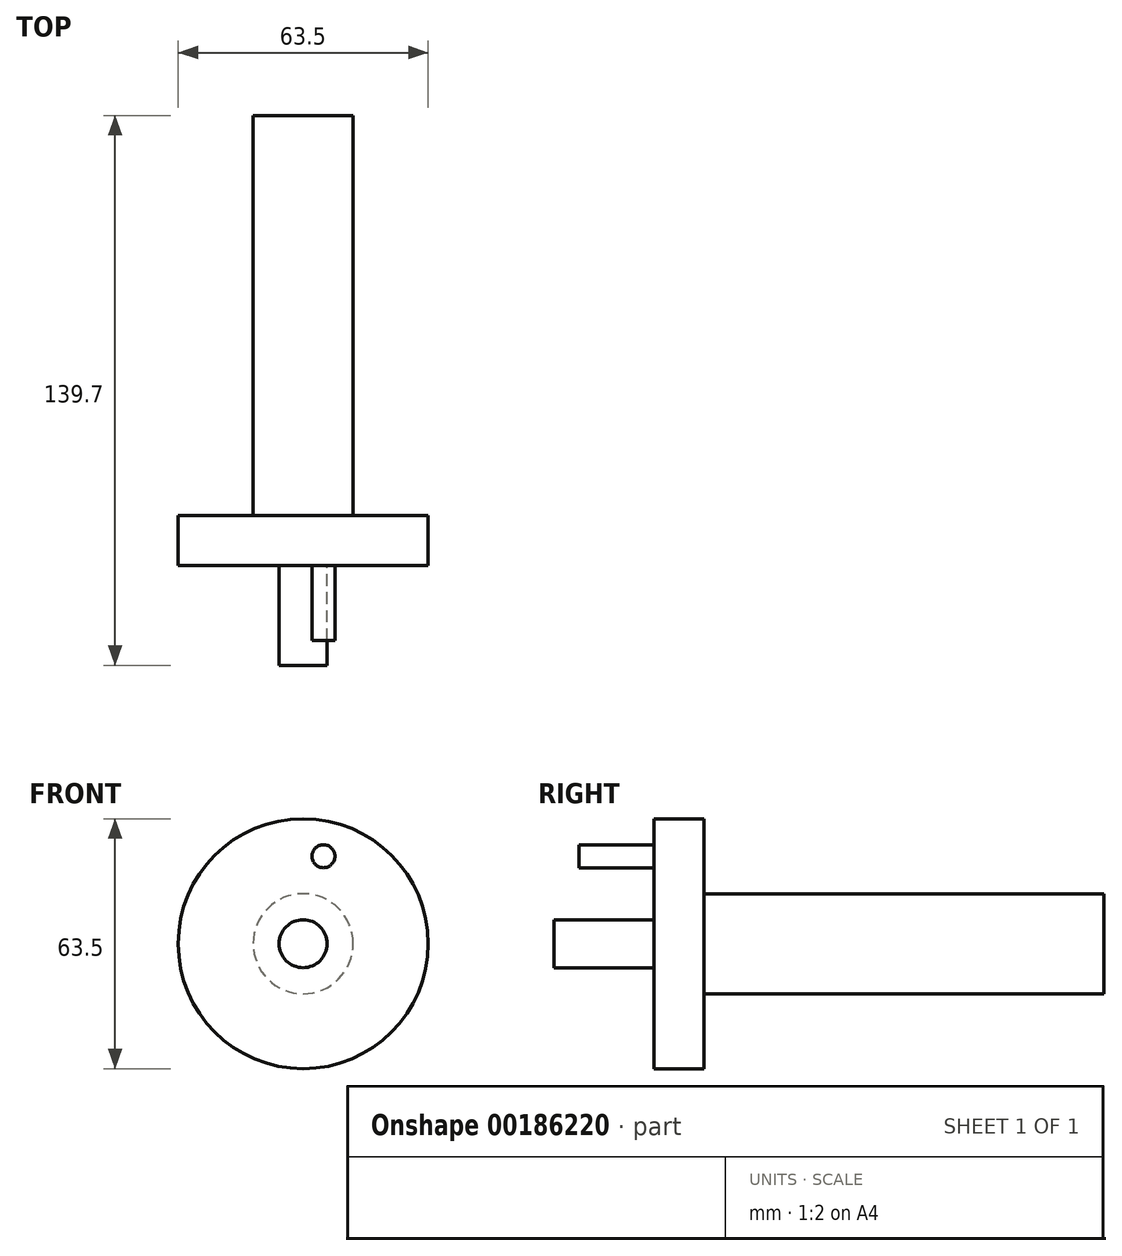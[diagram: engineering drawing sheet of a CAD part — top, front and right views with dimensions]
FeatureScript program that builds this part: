
annotation { "Feature Type Name" : "Feature", "Feature Type Description" : "" }
export const myFeature = defineFeature(function(context is Context, id is Id, definition is map)
    precondition{}
    {
        {
            var Q0;
            Q0=qCreatedBy(makeId("Front.planeOp"),FACE);
            var sketch = newSketch(context, id + "F0", { "sketchPlane" : qUnion([Q0])});
            skCircle(sketch, "E0", {"center": v(0, 0) * mm, "radius": 31.75 * mm});
            skSolve(sketch);
        }
        {
            var Q0;
            Q0=makeQuery(id+"F0.imprint","IMPRINT",FACE,{"disambiguationData":[TD([[makeQuery(id+"F0.imprint","IMPRINT",EDGE,{"derivedFrom":sQuery(id+"F0.wireOp",EDGE,"E0")}),1.0]])]});
            extrude(context, id + "F1", {"entities" : qUnion([Q0]), "depth" : 12.7 * mm});
        }
        {
            var Q0;
            Q0=qCreatedBy(makeId("Top.planeOp"),FACE);
            var sketch = newSketch(context, id + "F2", { "sketchPlane" : qUnion([Q0])});
            skLineSegment(sketch, "E1", {"start": v(0, 0) * mm, "end": v(0, -44.29) * mm, "construction": true});
            skSolve(sketch);
        }
        {
            var Q0;
            Q0=makeQuery(id+"F1.opExtrude","CAP_FACE",FACE,{"disambiguationData":[OSD([sQuery(id+"F0.wireOp",EDGE,"E0")])],"isStart":false});
            var sketch = newSketch(context, id + "F3", { "sketchPlane" : qUnion([Q0])});
            skCircle(sketch, "E2", {"center": v(0, 0) * mm, "radius": 6.1 * mm});
            skSolve(sketch);
        }
        {
            var Q0;
            Q0=makeQuery(id+"F3.imprint","IMPRINT",FACE,{"disambiguationData":[TD([[makeQuery(id+"F3.imprint","IMPRINT",EDGE,{"derivedFrom":sQuery(id+"F3.wireOp",EDGE,"E2")}),1.0]])]});
            extrude(context, id + "F4", {"entities" : qUnion([Q0]), "operationType" : NewBodyOperationType.ADD, "depth" : 25.4 * mm});
        }
        {
            var Q0;
            Q0=makeQuery(id+"F1.opExtrude","CAP_FACE",FACE,{"disambiguationData":[OSD([sQuery(id+"F0.wireOp",EDGE,"E0")])],"isStart":false});
            var sketch = newSketch(context, id + "F5", { "sketchPlane" : qUnion([Q0])});
            skCircle(sketch, "E3", {"center": v(5.14, 22.23) * mm, "radius": 2.92 * mm});
            skSolve(sketch);
        }
        {
            var Q0;
            Q0 = qSketchRegion(id + "F5", true);
            extrude(context, id + "F6", {"entities" : qUnion([Q0]), "operationType" : NewBodyOperationType.ADD, "depth" : 19.05 * mm});
        }
        {
            var Q0;
            Q0=qCreatedBy(makeId("Right.planeOp"),FACE);
            var sketch = newSketch(context, id + "F7", { "sketchPlane" : qUnion([Q0])});
            skFitSpline(sketch, "E4", {"points": [v(0, 22.05) * mm, v(18.8, 17.09) * mm, v(23.51, 0) * mm], "startDerivative": vector(86.62, 5.1) * mm, "endDerivative": vector(18.56, -94.88) * mm});
            skLineSegment(sketch, "E5", {"start": v(23.51, 0) * mm, "end": v(0, 0) * mm, "construction": true});
            skLineSegment(sketch, "E6", {"start": v(0, 0) * mm, "end": v(0, 22.05) * mm});
            skSolve(sketch);
        }
        {
            var Q0;
            Q0=sQuery(id+"F7.wireOp",EDGE,"E4");
            var Q1;
            Q1=sQuery(id+"F7.wireOp",EDGE,"E5");
            revolve(context, id + "F8", {"bodyType" : ToolBodyType.SURFACE, "surfaceEntities" : qUnion([Q0]), "axis" : qUnion([Q1]), "revolveType" : RevolveType.FULL});
        }
        {
            var Q0;
            Q0=makeQuery(id+"F1.opExtrude","CAP_FACE",FACE,{"disambiguationData":[OSD([sQuery(id+"F0.wireOp",EDGE,"E0")])],"isStart":true});
            var sketch = newSketch(context, id + "F9", { "sketchPlane" : qUnion([Q0])});
            skCircle(sketch, "E7", {"center": v(0, 0) * mm, "radius": 12.7 * mm});
            skSolve(sketch);
        }
        {
            var Q0;
            Q0=makeQuery(id+"F9.imprint","IMPRINT",FACE,{"disambiguationData":[TD([[makeQuery(id+"F9.imprint","IMPRINT",EDGE,{"derivedFrom":sQuery(id+"F9.wireOp",EDGE,"E7")}),1.0]])]});
            extrude(context, id + "F10", {"entities" : qUnion([Q0]), "operationType" : NewBodyOperationType.ADD, "depth" : 101.6 * mm});
        }
    });
